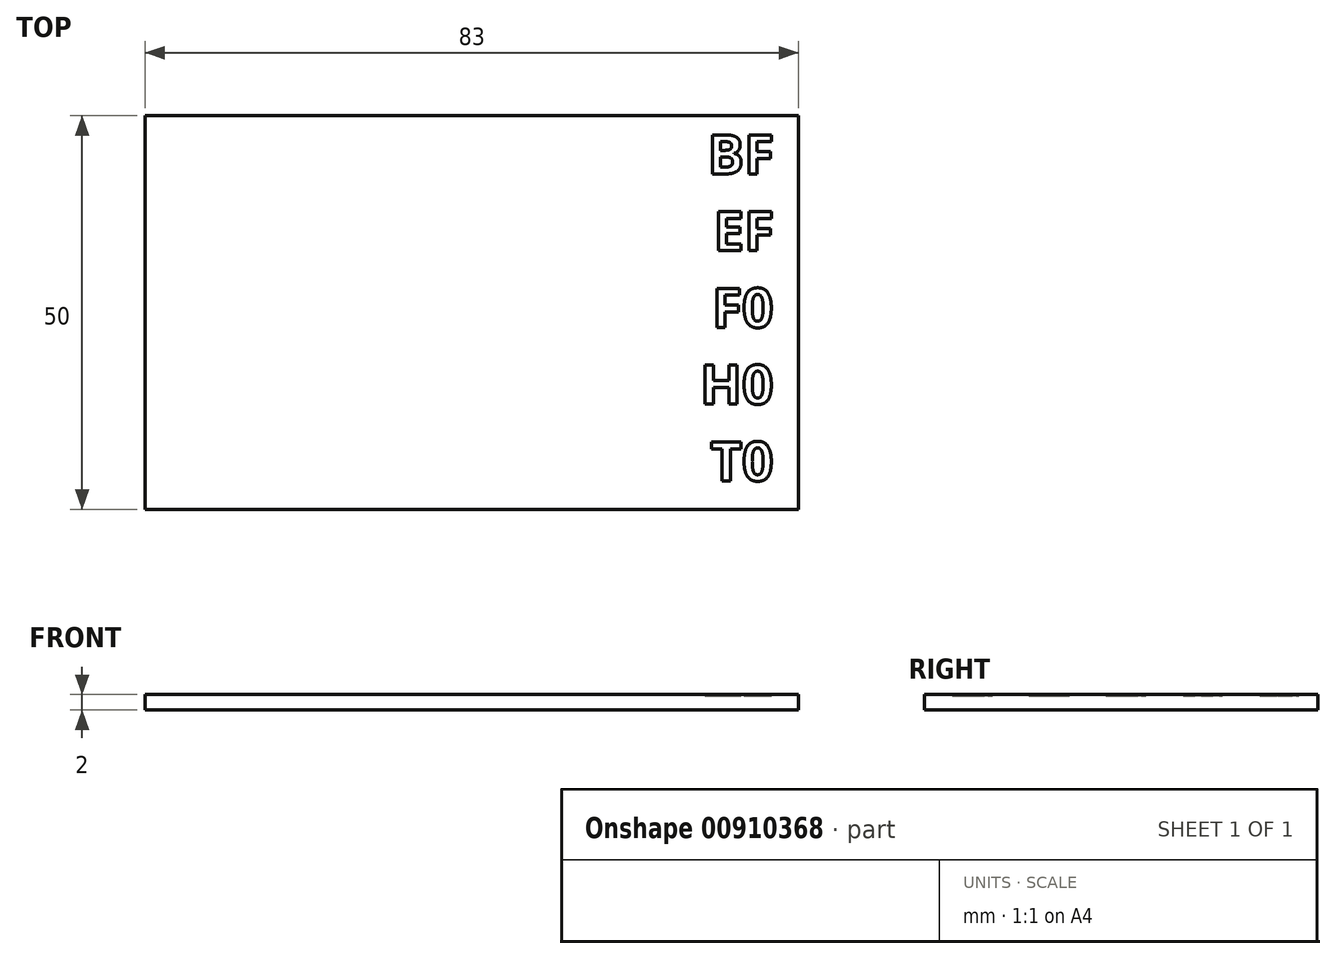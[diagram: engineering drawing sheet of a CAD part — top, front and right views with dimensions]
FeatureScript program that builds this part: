
annotation { "Feature Type Name" : "Feature", "Feature Type Description" : "" }
export const myFeature = defineFeature(function(context is Context, id is Id, definition is map)
    precondition{}
    {
        {
            var Q0;
            Q0=qCreatedBy(makeId("Top.planeOp"),FACE);
            var sketch = newSketch(context, id + "F0", { "sketchPlane" : qUnion([Q0])});
            skLineSegment(sketch, "E0.bottom", {"start": v(0, 0) * mm, "end": v(-83, 0) * mm});
            skLineSegment(sketch, "E0.top", {"start": v(0, 50) * mm, "end": v(-83, 50) * mm});
            skLineSegment(sketch, "E0.left", {"start": v(0, 0) * mm, "end": v(0, 50) * mm});
            skLineSegment(sketch, "E0.right", {"start": v(-83, 0) * mm, "end": v(-83, 50) * mm});
            skSolve(sketch);
        }
        {
            var Q0;
            Q0 = qSketchRegion(id + "F0", true);
            extrude(context, id + "F1", {"entities" : qUnion([Q0]), "depth" : 2 * mm, "offsetDistance" : 25.4 * mm});
        }
        {
            var Q0;
            Q0=makeQuery(id+"F1.opExtrude","CAP_FACE",FACE,{"disambiguationData":[OSD([sQuery(id+"F0.wireOp",EDGE,"E0.bottom"),sQuery(id+"F0.wireOp",EDGE,"E0.top"),sQuery(id+"F0.wireOp",EDGE,"E0.left"),sQuery(id+"F0.wireOp",EDGE,"E0.right")])],"isStart":false});
            var sketch = newSketch(context, id + "F2", { "sketchPlane" : qUnion([Q0])});
            skText(sketch, "E1", { "text": "BF", "fontName": "OpenSans-Bold.ttf"});
            skText(sketch, "E2", { "text": "EF", "fontName": "OpenSans-Bold.ttf"});
            skText(sketch, "E3", { "text": "F0", "fontName": "OpenSans-Bold.ttf"});
            skText(sketch, "E4", { "text": "H0", "fontName": "OpenSans-Bold.ttf"});
            skText(sketch, "E5", { "text": "T0", "fontName": "OpenSans-Bold.ttf"});
            skLineSegment(sketch, "E6", {"start": v(-3, 42.62) * mm, "end": v(-3, 37.87) * mm, "construction": true});
            skLineSegment(sketch, "E7", {"start": v(-3, 32.87) * mm, "end": v(-3, 28.12) * mm, "construction": true});
            skLineSegment(sketch, "E8", {"start": v(-3, 23.12) * mm, "end": v(-3, 18.37) * mm, "construction": true});
            skLineSegment(sketch, "E9", {"start": v(-3, 13.37) * mm, "end": v(-3, 8.62) * mm, "construction": true});
            skLineSegment(sketch, "E10", {"start": v(-3, 45.12) * mm, "end": v(0, 45.12) * mm, "construction": true});
            const initialGuessF2  = {"E1": [-0.01158, 0.04262, 1, 0, 0.005], "E2": [-0.0108, 0.03287, 1, 0, 0.005], "E3": [-0.01098, 0.02312, 1, 0, 0.005], "E4": [-0.01248, 0.01337, 1, 0, 0.005], "E5": [-0.01119, 0.00362, 1, 0, 0.005]};
            skSetInitialGuess(sketch, initialGuessF2);
            skSolve(sketch);
        }
        {
            var Q0;
            Q0 = qSketchRegion(id + "F2", true);
            extrude(context, id + "F3", {"entities" : qUnion([Q0]), "operationType" : NewBodyOperationType.REMOVE, "oppositeDirection" : true, "depth" : .2 * mm, "offsetDistance" : 25.4 * mm});
        }
    });
